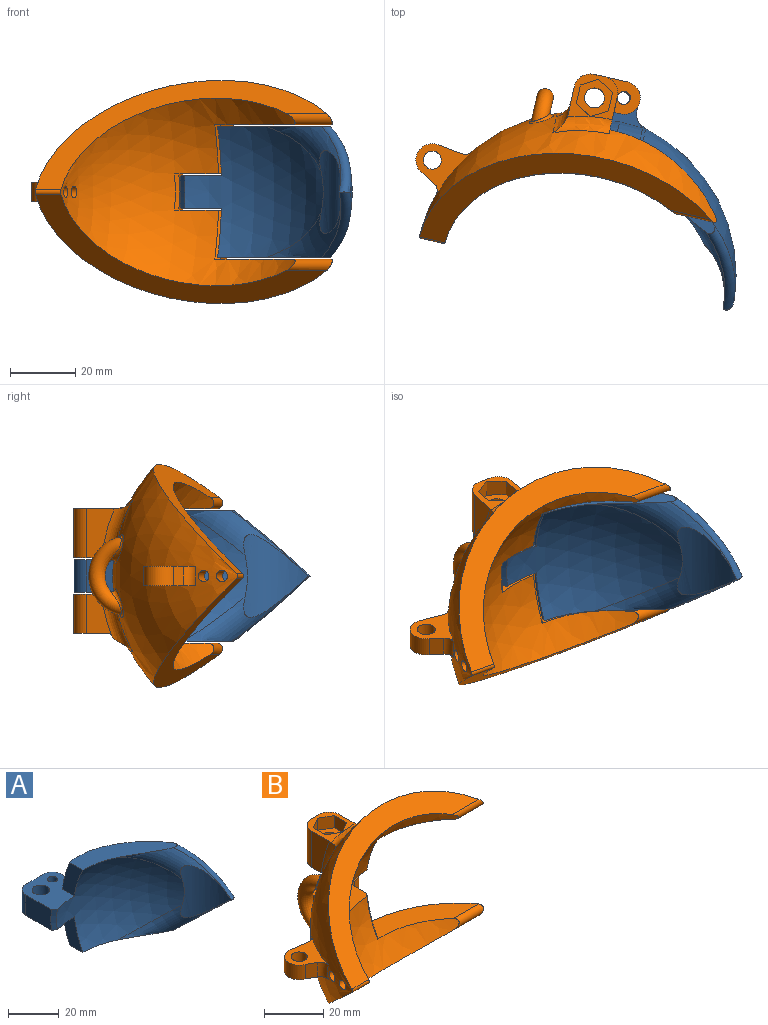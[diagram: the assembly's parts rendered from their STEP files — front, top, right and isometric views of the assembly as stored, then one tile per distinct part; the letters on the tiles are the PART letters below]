
ASSEMBLY  parts=2 mates=1
PART A: 28 faces, bbox 68.3x60.5x69.5 mm
  f0: cone r=48.87mm half-angle=1.5deg, axis (-1,0,0), area 114.2mm2, adj f6,f9,f21,f27
  f1: sphere r=50mm, area 2062mm2, adj f3,f6,f8,f9,f12,f13,f24,f26
  f2: sphere r=42mm, area 1673.3mm2, adj f3,f4,f5,f6,f8,f9,f10,f11
  f3: plane 24.14x20.92mm, normal (0,0,1), area 286.7mm2, adj f1,f2,f4,f7,f15,f16,f17,f18
  f4: plane 15x11.44mm, normal (-1,0,0), area 104.2mm2, adj f2,f3,f8,f22
  f5: plane 15x11.44mm, normal (-1,0,0), area 104.2mm2, adj f2,f6,f9,f21
  f6: plane 24.14x20.92mm, normal (0,0,-1), area 286.7mm2, adj f0,f1,f2,f5,f7,f15,f16,f17
  f7: plane 14.41x10mm, normal (-1,0,0), area 142.1mm2, adj f3,f6,f19,f25
  f8: plane 38.82x22.55mm, normal (0,0,1), area 333.8mm2, adj f1,f2,f4,f10,f12,f22,f23,f26
  f9: plane 38.82x22.55mm, normal (0,0,-1), area 333.8mm2, adj f0,f1,f2,f5,f11,f13,f21,f27
  f10: torus R=51.04mm, axis (0,0.68,-0.73), area 183.4mm2, adj f2,f8,f12,f14
  f11: torus R=51.04mm, axis (0,0.68,0.73), area 183.5mm2, adj f2,f9,f13,f14
  f12: torus R=47.93mm, axis (0,-0.68,0.73), area 128.7mm2, adj f1,f8,f10,f13
  f13: torus R=47.93mm, axis (0,-0.68,-0.73), area 128.7mm2, adj f1,f9,f11,f12
  f14: cylinder r=22.17mm len=25.3mm, axis (0,0,1), area 330.4mm2, adj f2,f10,f11
  f15: plane 10x10mm, normal (0,1,0), area 100mm2, adj f3,f6,f18,f19
  f16: cylinder r=3.5mm len=10mm, axis (0,0,-1), area 219.9mm2, adj f3,f6
  f17: plane 10x2.57mm, normal (1,0,0), area 24.2mm2, adj f3,f6,f18,f24
  f18: cylinder r=5mm len=10mm, axis (0,0,1), area 78.5mm2, adj f3,f6,f15,f17
  f19: cylinder r=5mm len=10mm, axis (0,0,1), area 78.5mm2, adj f3,f6,f7,f15
  f20: cylinder r=2mm len=10mm, axis (0,0,-1), area 125.7mm2, adj f3,f6
  f21: cone r=49.62mm half-angle=9.2deg, axis (1,0,0), area 43.4mm2, adj f0,f5,f6,f9
  f22: cone r=49.62mm half-angle=9.2deg, axis (1,0,0), area 43.4mm2, adj f3,f4,f8,f23
  f23: cone r=48.87mm half-angle=1.5deg, axis (-1,0,0), area 114.2mm2, adj f3,f8,f22,f26
  f24: torus R=53.66mm, axis (1,0,0), area 63.5mm2, adj f1,f3,f6,f17
  f25: cone r=40.49mm half-angle=37.3deg, axis (-1,0,0), area 23.2mm2, adj f2,f3,f6,f7
  f26: torus R=43.89mm, axis (-1,0,0), area 15.4mm2, adj f1,f3,f8,f23
  f27: torus R=43.89mm, axis (-1,0,0), area 15.4mm2, adj f0,f1,f6,f9
PART B: 68 faces, bbox 93.8x60.8x68.3 mm
  f0: plane 17.69x17.69mm, normal (1,0,0), area 169.6mm2, adj f6,f13,f14,f21,f22,f29,f33,f61
  f1: plane 12.86x7.79mm, normal (-1,0,0), area 69.9mm2, adj f13,f25,f31,f61,f65
  f2: cylinder r=3.05mm len=12mm, axis (0,0,-1), area 230mm2, adj f13,f61
  f3: plane 14.34x13.54mm, normal (0,0,1), area 76.1mm2, adj f5,f10,f16,f17,f26,f30,f32,f42
  f4: cylinder r=3.05mm len=10mm, axis (0,0,-1), area 191.6mm2, adj f11,f48
  f5: torus R=48.73mm, axis (0,0,-1), area 82.1mm2, adj f3,f6,f10,f32,f46,f47
  f6: sphere r=50mm, area 3695mm2, adj f0,f5,f7,f9,f10,f11,f13,f14
  f7: plane 85.56x35.78mm, normal (0,-0.68,0.73), area 826.9mm2, adj f6,f8,f37,f59
  f8: sphere r=42mm, area 2819.8mm2, adj f7,f9,f11,f13,f14,f15,f33,f34
  f9: plane 85.56x35.78mm, normal (0,-0.68,-0.73), area 826.9mm2, adj f6,f8,f38,f59
  f10: plane 17.7x17.69mm, normal (1,0,0), area 193.4mm2, adj f3,f5,f6,f11,f15,f19,f20,f30
  f11: plane 23.87x22.24mm, normal (0,0,-1), area 288.6mm2, adj f4,f6,f8,f10,f12,f16,f17,f20
  f12: plane 11x5.69mm, normal (1,0,0), area 58.6mm2, adj f11,f13,f35,f36
  f13: plane 23.87x22.24mm, normal (0,0,1), area 288.6mm2, adj f0,f1,f2,f6,f8,f12,f18,f22
  f14: plane 38.65x18.56mm, normal (0,0,1), area 319mm2, adj f0,f6,f8,f33,f38
  f15: plane 38.65x18.56mm, normal (0,0,-1), area 319mm2, adj f6,f8,f10,f34,f37
  f16: plane 15x10.5mm, normal (0,1,0), area 94.5mm2, adj f3,f11,f19,f24,f26,f30
  f17: plane 15x8.63mm, normal (-1,0,0), area 93.8mm2, adj f3,f11,f26,f32
  f18: plane 12x10.5mm, normal (0,1,0), area 84mm2, adj f13,f21,f23,f25,f29,f61
  f19: plane 12x10mm, normal (0,0,1), area 52.1mm2, adj f10,f16,f20,f24,f28,f30
  f20: plane 6x2mm, normal (0,-1,0), area 12mm2, adj f10,f11,f19,f24
  f21: plane 12x10mm, normal (0,0,-1), area 52.1mm2, adj f0,f18,f22,f23,f27,f29
  f22: plane 6x2mm, normal (0,-1,0), area 12mm2, adj f0,f13,f21,f23
  f23: cylinder r=5mm len=10mm, axis (0,0,1), area 94.2mm2, adj f13,f18,f21,f22
  f24: cylinder r=5mm len=10mm, axis (0,0,1), area 94.2mm2, adj f11,f16,f19,f20
  f25: cylinder r=5mm len=12mm, axis (0,0,-1), area 94.2mm2, adj f1,f13,f18,f61
  f26: cylinder r=5mm len=15mm, axis (0,0,-1), area 117.8mm2, adj f3,f11,f16,f17
  f27: cylinder r=2mm len=6mm, axis (0,0,-1), area 75.4mm2, adj f13,f21
  f28: cylinder r=2mm len=6mm, axis (0,0,-1), area 75.4mm2, adj f11,f19
  f29: cylinder r=5mm len=6mm, axis (0,0,-1), area 47.1mm2, adj f0,f18,f21,f61
  f30: cylinder r=5mm len=9mm, axis (0,0,-1), area 70.7mm2, adj f3,f10,f16,f19
  f31: torus R=51.61mm, axis (-1,0,0), area 99mm2, adj f1,f6,f13,f62,f65
  f32: torus R=51.61mm, axis (1,0,0), area 101.1mm2, adj f3,f5,f6,f11,f17
  f33: cone r=41.96mm half-angle=46.3deg, axis (1,0,0), area 32.9mm2, adj f0,f8,f13,f14
  f34: cone r=41.96mm half-angle=46.3deg, axis (1,0,0), area 32.9mm2, adj f8,f10,f11,f15
  f35: cone r=40.64mm half-angle=55.4deg, axis (1,0,0), area 18.8mm2, adj f8,f11,f12,f13
  f36: cone r=47.38mm half-angle=35.7deg, axis (-1,0,0), area 26.9mm2, adj f6,f11,f12,f13
  f37: cylinder r=2mm len=13.7mm, axis (1,0,0), area 58.7mm2, adj f6,f7,f8,f15
  f38: cylinder r=2mm len=13.7mm, axis (-1,0,0), area 58.7mm2, adj f6,f8,f9,f14
  f39: torus R=9.66mm, axis (-1,0,0), area 349.8mm2, adj f40,f41
  f40: bspline ~8.83x6.86mm, area 36.5mm2, adj f6,f39
  f41: bspline ~8.83x6.87mm, area 36.5mm2, adj f6,f39
  f42: plane 5.83x5mm, normal (-1,0,0), area 29.2mm2, adj f3,f43,f46,f48
  f43: plane 5.05x5mm, normal (-0.5,-0.87,0), area 29.2mm2, adj f3,f42,f44,f48
  f44: plane 5.05x5mm, normal (0.5,-0.87,0), area 29.2mm2, adj f3,f43,f45,f48
  f45: plane 5.83x5mm, normal (1,0,0), area 29.2mm2, adj f3,f44,f47,f48
  f46: plane 5.05x5mm, normal (-0.5,0.87,0), area 29.2mm2, adj f3,f5,f42,f47,f48
  f47: plane 5.05x5mm, normal (0.5,0.87,0), area 29.2mm2, adj f3,f5,f45,f46,f48
  f48: plane 11.66x10.1mm, normal (0,0,1), area 59.1mm2, adj f4,f42,f43,f44,f45,f46,f47
  f49: plane 7.66x6mm, normal (0.14,0.99,0), area 46mm2, adj f50,f53,f54,f55
  f50: cylinder r=5mm len=9.68mm, axis (0,0,-1), area 87.6mm2, adj f49,f51,f53,f54
  f51: plane 6x3.83mm, normal (-0.48,-0.88,0), area 25.9mm2, adj f50,f53,f54,f56
  f52: cylinder r=2.75mm len=6mm, axis (0,0,-1), area 103.7mm2, adj f53,f54
  f53: plane 16.22x15.43mm, normal (0,0,1), area 100mm2, adj f6,f49,f50,f51,f52,f55,f56
  f54: plane 16.22x15.43mm, normal (0,0,-1), area 100mm2, adj f6,f49,f50,f51,f52,f55,f56
  f55: torus R=46.57mm, axis (-0.14,-0.99,0), area 19.3mm2, adj f6,f49,f53,f54
  f56: torus R=51.78mm, axis (0.48,0.88,0), area 24.3mm2, adj f6,f51,f53,f54
  f57: cylinder r=1.75mm len=8.49mm, axis (1,0,0), area 88.7mm2, adj f6,f8
  f58: cylinder r=1.75mm len=9.19mm, axis (1,0,0), area 91mm2, adj f6,f8
  f59: cylinder r=1mm len=8mm, axis (1,0,0), area 13.1mm2, adj f6,f7,f8,f9
  f60: cylinder r=8mm len=5.99mm, axis (0,0,-1), area 3.4mm2, adj f61,f65,f66,f67
  f61: plane 15x13.5mm, normal (0,0,-1), area 149.5mm2, adj f0,f1,f2,f18,f25,f29,f60,f65
  f62: torus R=48.73mm, axis (0,0,-1), area 16.6mm2, adj f6,f31,f63,f65
  f63: bspline ~11.75x6.31mm, area 14.7mm2, adj f6,f62,f64,f66
  f64: torus R=48.73mm, axis (0,0,-1), area 1.4mm2, adj f0,f6,f63,f67
  f65: bspline ~10.24x6.36mm, area 22mm2, adj f1,f31,f60,f61,f62,f66
  f66: bspline ~10.16x4.05mm, area 30.5mm2, adj f60,f63,f65,f67
  f67: bspline ~8.36x6.27mm, area 10.7mm2, adj f0,f60,f61,f64,f66
PLACE A rot(axis=(0,0,-1),14deg) t=(-22.53,-38.29,17.77)mm
PLACE B rot(axis=(0,0,-1),12.8deg) t=(-20.7,-38.58,17.77)mm fixed
MATE revolute A.f16 <-> B.f2  axis (0,0,1) through (-15.8,15.68,22.77)mm
